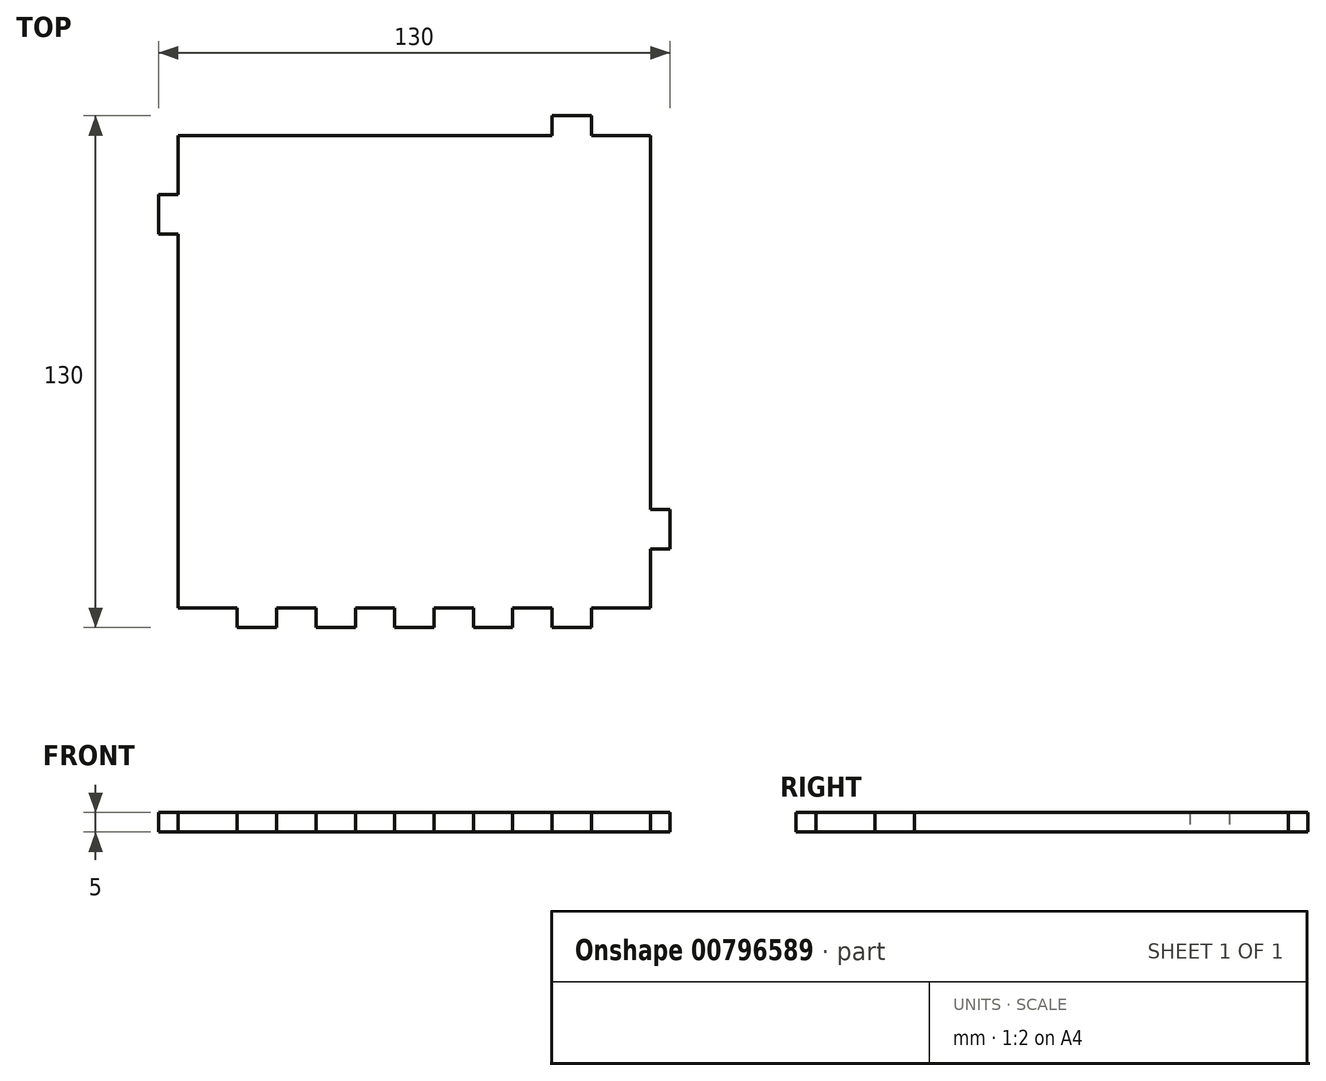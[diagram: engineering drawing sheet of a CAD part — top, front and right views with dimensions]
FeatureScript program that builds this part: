
annotation { "Feature Type Name" : "Feature", "Feature Type Description" : "" }
export const myFeature = defineFeature(function(context is Context, id is Id, definition is map)
    precondition{}
    {
        {
            var Q0;
            Q0=qCreatedBy(makeId("Top.planeOp"),FACE);
            var sketch = newSketch(context, id + "F0", { "sketchPlane" : qUnion([Q0])});
            skLineSegment(sketch, "E0.bottom", {"start": v(60, 60) * mm, "end": v(-60, 60) * mm});
            skLineSegment(sketch, "E0.top", {"start": v(60, -60) * mm, "end": v(-60, -60) * mm});
            skLineSegment(sketch, "E0.left", {"start": v(60, 60) * mm, "end": v(60, -60) * mm});
            skLineSegment(sketch, "E0.right", {"start": v(-60, 60) * mm, "end": v(-60, -60) * mm});
            skPoint(sketch, "E0.middle", {"position": v(0, 0) * mm});
            skLineSegment(sketch, "E1.bottom", {"start": v(-45, -60) * mm, "end": v(-35, -60) * mm});
            skLineSegment(sketch, "E1.top", {"start": v(-45, -65) * mm, "end": v(-35, -65) * mm});
            skLineSegment(sketch, "E1.left", {"start": v(-45, -60) * mm, "end": v(-45, -65) * mm});
            skLineSegment(sketch, "E1.right", {"start": v(-35, -60) * mm, "end": v(-35, -65) * mm});
            skLineSegment(sketch, "E2.1.0.0", {"start": v(-15, -60) * mm, "end": v(-15, -65) * mm});
            skLineSegment(sketch, "E2.1.0.1", {"start": v(-25, -60) * mm, "end": v(-25, -65) * mm});
            skLineSegment(sketch, "E2.1.0.2", {"start": v(-25, -65) * mm, "end": v(-15, -65) * mm});
            skLineSegment(sketch, "E2.2.0.0", {"start": v(5, -60) * mm, "end": v(5, -65) * mm});
            skLineSegment(sketch, "E2.2.0.1", {"start": v(-5, -60) * mm, "end": v(-5, -65) * mm});
            skLineSegment(sketch, "E2.2.0.2", {"start": v(-5, -65) * mm, "end": v(5, -65) * mm});
            skLineSegment(sketch, "E2.3.0.0", {"start": v(25, -60) * mm, "end": v(25, -65) * mm});
            skLineSegment(sketch, "E2.3.0.1", {"start": v(15, -60) * mm, "end": v(15, -65) * mm});
            skLineSegment(sketch, "E2.3.0.2", {"start": v(15, -65) * mm, "end": v(25, -65) * mm});
            skLineSegment(sketch, "E2.4.0.0", {"start": v(45, -60) * mm, "end": v(45, -65) * mm});
            skLineSegment(sketch, "E2.4.0.1", {"start": v(35, -60) * mm, "end": v(35, -65) * mm});
            skLineSegment(sketch, "E2.4.0.2", {"start": v(35, -65) * mm, "end": v(45, -65) * mm});
            skLineSegment(sketch, "E2.direction1", {"start": v(-45, -65) * mm, "end": v(-25, -65) * mm, "construction": true});
            skLineSegment(sketch, "E3.1.0", {"start": v(60, -45) * mm, "end": v(65, -45) * mm});
            skLineSegment(sketch, "E3.1.1", {"start": v(60, -35) * mm, "end": v(65, -35) * mm});
            skLineSegment(sketch, "E3.1.2", {"start": v(65, -45) * mm, "end": v(65, -35) * mm});
            skLineSegment(sketch, "E4.2.2.0", {"start": v(45, 60) * mm, "end": v(45, 65) * mm});
            skLineSegment(sketch, "E4.3.2.0", {"start": v(35, 60) * mm, "end": v(35, 65) * mm});
            skLineSegment(sketch, "E4.6.2.0", {"start": v(45, 65) * mm, "end": v(35, 65) * mm});
            skLineSegment(sketch, "E5.2.3.0", {"start": v(-60, 45) * mm, "end": v(-65, 45) * mm});
            skLineSegment(sketch, "E5.3.3.0", {"start": v(-60, 35) * mm, "end": v(-65, 35) * mm});
            skLineSegment(sketch, "E5.6.3.0", {"start": v(-65, 45) * mm, "end": v(-65, 35) * mm});
            skSolve(sketch);
        }
        {
            var Q0;
            Q0 = qSketchRegion(id + "F0", true);
            extrude(context, id + "F1", {"entities" : qUnion([Q0]), "depth" : 5 * mm, "offsetDistance" : 25 * mm});
        }
    });
